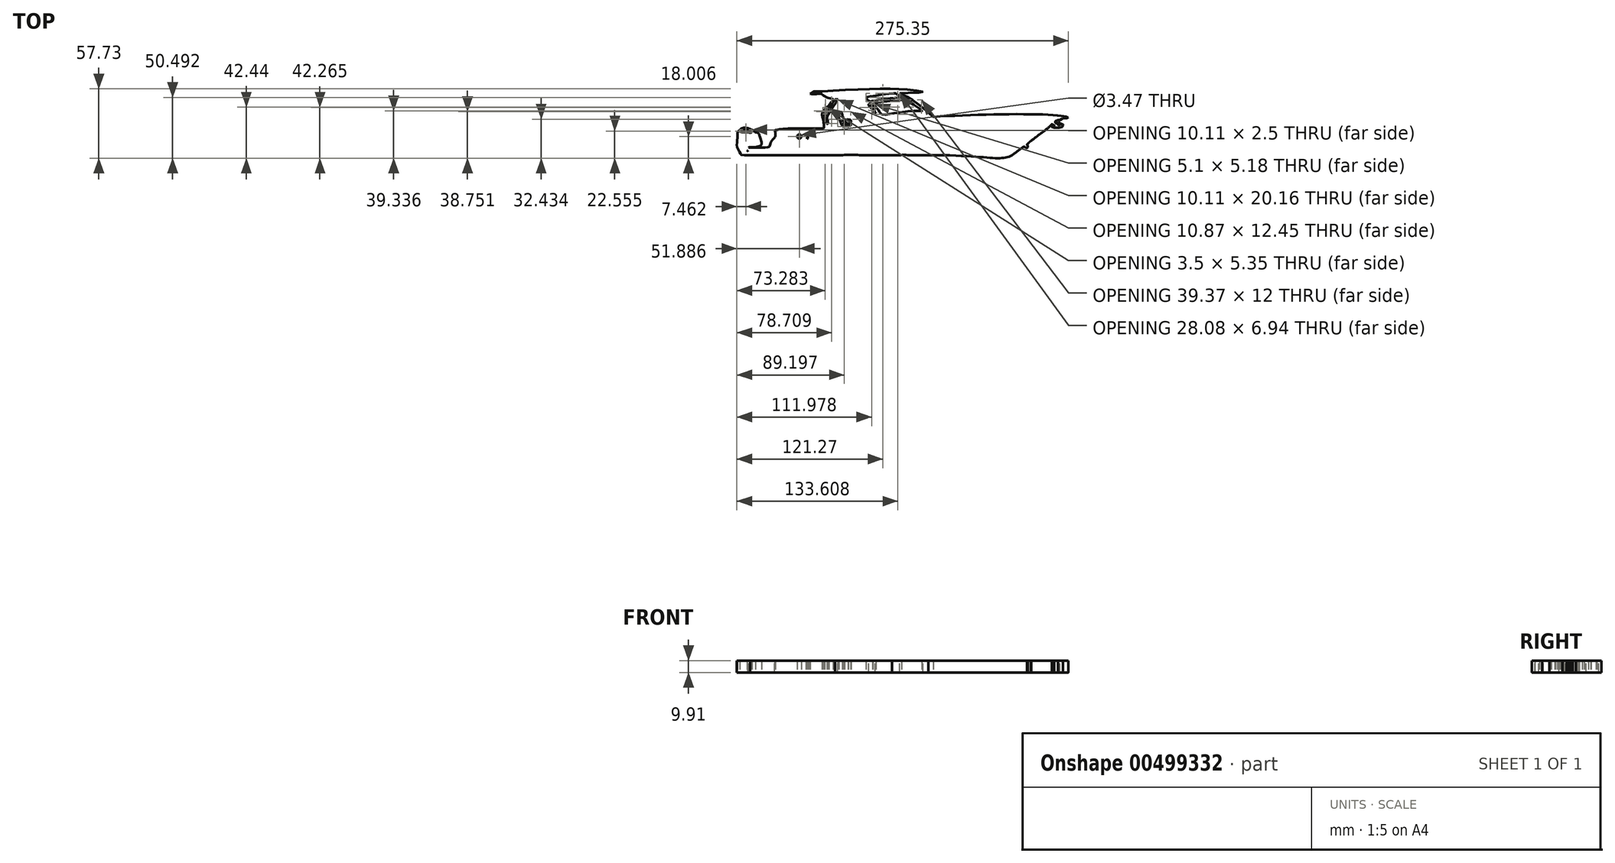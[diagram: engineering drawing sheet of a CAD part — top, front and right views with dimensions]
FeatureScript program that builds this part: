
annotation { "Feature Type Name" : "Feature", "Feature Type Description" : "" }
export const myFeature = defineFeature(function(context is Context, id is Id, definition is map)
    precondition{}
    {
        {
            var Q0;
            Q0=qCreatedBy(makeId("Top.planeOp"),FACE);
            var sketch = newSketch(context, id + "F0", { "sketchPlane" : qUnion([Q0])});
            skFitSpline(sketch, "E0", {"points": [v(181.82, 12.96) * mm, v(177.4, 14.1) * mm, v(69.7, 13.5) * mm, v(25.53, 9.3) * mm, v(19.92, 8.52) * mm], "startDerivative": vector(1.7, -4.6) * mm, "endDerivative": vector(-96.1, -9.77) * mm});
            skFitSpline(sketch, "E1", {"points": [v(19.92, 8.52) * mm, v(11.89, 7.3) * mm, v(0, 4.75) * mm, v(-5.76, 3.64) * mm, v(-21.62, 3.73) * mm, v(-57.86, 3.13) * mm, v(-62.13, 1.85) * mm, v(-60.42, 1.34) * mm, v(-58.8, 1) * mm, v(-52.92, 0.83) * mm, v(-44.65, 0.83) * mm, v(-38.6, 0.91) * mm, v(-28.44, 1) * mm, v(-16.08, 0.83) * mm, v(-10.37, 0.91) * mm, v(-5.5, 0.91) * mm, v(-2.78, 1.42) * mm, v(1.49, 2.79) * mm, v(4.56, 3.64) * mm, v(10.7, 4.66) * mm, v(15.39, 5.6) * mm, v(20.67, 6.46) * mm, v(27.84, 7.48) * mm, v(53.16, 10.3) * mm, v(65.53, 10.8) * mm, v(70.56, 11.23) * mm, v(181.82, 12.96) * mm], "startDerivative": vector(-204.32, -26.46) * mm, "endDerivative": vector(1116.59, 11.05) * mm});
            skFitSpline(sketch, "E2", {"points": [v(150.8, -6.4) * mm, v(136.83, -7.24) * mm, v(77, -11.4) * mm, v(39.07, -13.62) * mm, v(-5.53, -13.97) * mm, v(-32.22, -13.7) * mm, v(-56.7, -13.54) * mm, v(-83.8, -13.7) * mm, v(-84.92, -14.48) * mm, v(-83.04, -15.59) * mm, v(-76.47, -15.59) * mm, v(-57.71, -15.59) * mm, v(-38.53, -16.01) * mm, v(-32.64, -16.01) * mm, v(-7.32, -16.01) * mm, v(12.55, -15.84) * mm, v(72.24, -13.54) * mm, v(94.33, -11.75) * mm, v(106.35, -10.81) * mm, v(150.8, -6.4) * mm]});
            skFitSpline(sketch, "E3", {"points": [v(-62.13, 1.85) * mm, v(-61.49, 0.78) * mm, v(-61.61, -2.84) * mm, v(-63.48, -5.07) * mm, v(-65.9, -9.53) * mm, v(-67.22, -11.64) * mm, v(-83.62, -12) * mm, v(-83.38, -12.3) * mm, v(-83.8, -13.7) * mm], "startDerivative": vector(9.33, -10.43) * mm, "endDerivative": vector(-10.89, -19.72) * mm});
            skFitSpline(sketch, "E4", {"points": [v(-83.62, -12) * mm, v(-73.48, -10.16) * mm, v(-74.45, -2.78) * mm, v(-77.88, 0.76) * mm], "startDerivative": vector(4.15, 3.72) * mm, "endDerivative": vector(-38.38, 8.76) * mm});
            skFitSpline(sketch, "E5", {"points": [v(-77.88, 0.76) * mm, v(-79.82, 1.87) * mm, v(-83.38, 3.86) * mm, v(-86.1, 4.58) * mm, v(-88.98, 3.98) * mm, v(-91.58, 2.29) * mm, v(-92.7, 0.76) * mm, v(-92.95, -2.8) * mm, v(-93.16, -6.9) * mm, v(-93.43, -10.58) * mm, v(-92.18, -13.75) * mm, v(-90.43, -17.3) * mm, v(-89.7, -18.23) * mm, v(-82.47, -18.23) * mm, v(-82.35, -18.23) * mm], "startDerivative": vector(-35.29, 17.01) * mm, "endDerivative": vector(3.35, -0.6) * mm});
            skFitSpline(sketch, "E6", {"points": [v(-84.92, -14.48) * mm, v(-83.04, -16.64) * mm, v(-82.35, -18.23) * mm], "startDerivative": vector(4.12, -3.97) * mm, "endDerivative": vector(0.95, -4.82) * mm});
            skFitSpline(sketch, "E7", {"points": [v(-80.95, 0.76) * mm, v(-88.13, 0.76) * mm, v(-91.05, 1.27) * mm, v(-89.24, 2.99) * mm, v(-80.95, 0.76) * mm]});
            skFitSpline(sketch, "E8", {"points": [v(149.26, -7.8) * mm, v(147.28, -7.83) * mm, v(113.55, -11.96) * mm, v(83.7, -15.93) * mm, v(65.63, -18.23) * mm, v(43.16, -18.23) * mm, v(35.36, -18.23) * mm, v(37.32, -17.46) * mm, v(40.05, -16.74) * mm, v(43.16, -16.7) * mm, v(43.2, -17.38) * mm], "startDerivative": vector(-28.19, 2) * mm, "endDerivative": vector(-7.93, -28.97) * mm});
            skFitSpline(sketch, "E9", {"points": [v(35.36, -18.23) * mm, v(6.92, -18.23) * mm, v(-5.49, -18.23) * mm, v(-12.01, -18.23) * mm, v(-9.45, -17.33) * mm, v(-8.43, -17.16) * mm, v(-5.53, -17.12) * mm], "startDerivative": vector(-93.99, -0.34) * mm, "endDerivative": vector(31.9, 0.18) * mm});
            skFitSpline(sketch, "E10", {"points": [v(-5.53, -17.12) * mm, v(-5.49, -18.23) * mm], "startDerivative": vector(0.04, -1.11) * mm, "endDerivative": vector(0.04, -1.11) * mm});
            skFitSpline(sketch, "E11", {"points": [v(-12.01, -18.23) * mm, v(-82.35, -18.23) * mm], "startDerivative": vector(-70.34, 0) * mm, "endDerivative": vector(-70.34, 0) * mm});
            skFitSpline(sketch, "E12", {"points": [v(-32.53, 32.61) * mm, v(-29.39, 34.74) * mm, v(-27.97, 34.64) * mm, v(-1.6, 35.86) * mm, v(31.66, 36.87) * mm, v(52.65, 35.66) * mm, v(60.76, 33.83) * mm, v(41.9, 33.02) * mm, v(43.22, 32.3) * mm, v(51.33, 27.95) * mm, v(61.47, 20.65) * mm, v(69.7, 13.5) * mm], "startDerivative": vector(69.06, 54.52) * mm, "endDerivative": vector(89.04, -78.05) * mm});
            skFitSpline(sketch, "E13", {"points": [v(-32.53, 32.61) * mm, v(-26.45, 32.61) * mm, v(-23.5, 32.61) * mm, v(-18.94, 29.77) * mm, v(-13.47, 27.98) * mm, v(-16.91, 22.68) * mm], "startDerivative": vector(30.81, -1.19) * mm, "endDerivative": vector(-8.73, -35.9) * mm});
            skFitSpline(sketch, "E14", {"points": [v(-16.91, 22.68) * mm, v(-19.75, 20.65) * mm, v(-22.6, 15.68) * mm, v(-21.98, 11.93) * mm, v(-21.17, 4.73) * mm, v(-21.62, 3.73) * mm], "startDerivative": vector(-14.92, -8.12) * mm, "endDerivative": vector(-5.25, -6.4) * mm});
            skFitSpline(sketch, "E15", {"points": [v(-18.44, 21.16) * mm, v(-20.8, 18.68) * mm, v(-22.04, 16.19) * mm, v(-21.62, 15.68) * mm, v(-20.23, 17.88) * mm, v(-18.44, 21.16) * mm]});
            skFitSpline(sketch, "E16", {"points": [v(-9.7, 27.98) * mm, v(-11.33, 27.98) * mm, v(-20.28, 13.5) * mm, v(-19.94, 11.75) * mm, v(-18.94, 7.75) * mm, v(-17.85, 7.92) * mm, v(-18.44, 11.84) * mm, v(-18.44, 13.5) * mm, v(-16.91, 16.62) * mm, v(-9.96, 27.1) * mm, v(-9.7, 27.98) * mm]});
            skFitSpline(sketch, "E17", {"points": [v(-9.7, 27.98) * mm, v(-5.44, 32.9) * mm, v(-3.74, 33.33) * mm, v(4.36, 33.24) * mm, v(6.07, 32.14) * mm, v(10.59, 28.8) * mm, v(12.12, 27.98) * mm, v(14.77, 25.31) * mm, v(15.8, 24.3) * mm, v(15.53, 23.18) * mm, v(17.58, 21.05) * mm, v(19.97, 19.09) * mm, v(22.19, 18.51) * mm, v(23.9, 16.79) * mm, v(19.37, 17.55) * mm, v(18.43, 16.79) * mm, v(15.36, 14.06) * mm, v(13.06, 12.52) * mm, v(8.46, 11.5) * mm, v(8.54, 10.05) * mm, v(8.37, 7.4) * mm, v(-4.85, 5.62) * mm, v(-5.61, 5.36) * mm], "startDerivative": vector(75.6, 96.22) * mm, "endDerivative": vector(-15.4, -12.16) * mm});
            skFitSpline(sketch, "E18", {"points": [v(-8.77, 17.8) * mm, v(-9.7, 16.87) * mm, v(-5.61, 5.36) * mm], "startDerivative": vector(-4.93, -2.36) * mm, "endDerivative": vector(8.91, -19.64) * mm});
            skFitSpline(sketch, "E19", {"points": [v(1.49, 2.79) * mm, v(10.57, 2.79) * mm, v(29.44, 2.79) * mm, v(48.6, 3.64) * mm, v(74.48, 3.64) * mm, v(166.01, 5.23) * mm], "startDerivative": vector(71.82, 0.39) * mm, "endDerivative": vector(290.97, 6.55) * mm});
            skFitSpline(sketch, "E20", {"points": [v(26.77, 15.59) * mm, v(34.58, 16.15) * mm, v(41.48, 17.07) * mm, v(55.63, 18.51) * mm, v(60.25, 18.51) * mm, v(48.31, 27.11) * mm, v(46.42, 27.9) * mm, v(19.37, 24.28) * mm, v(19.74, 23.5) * mm, v(22.19, 21.5) * mm, v(24.66, 18.51) * mm, v(26.77, 15.59) * mm]});
            skFitSpline(sketch, "E21", {"points": [v(13.76, 29.24) * mm, v(16.86, 26.33) * mm, v(18.89, 26.53) * mm, v(27.64, 28.2) * mm, v(41.98, 29.67) * mm, v(43.34, 30.05) * mm, v(38.46, 33.01) * mm, v(38.1, 33.25) * mm, v(14.63, 29.92) * mm, v(13.76, 29.24) * mm]});
            skFitSpline(sketch, "E22", {"points": [v(-8.77, 17.8) * mm, v(-7.56, 17.8) * mm, v(-6.18, 17.08) * mm, v(-5.74, 15.7) * mm, v(-5.85, 14.54) * mm, v(-5.43, 13.78) * mm, v(-4.73, 12.96) * mm, v(-4.47, 12.29) * mm, v(-4.18, 10.85) * mm, v(-4.5, 10.05) * mm, v(-5.42, 9.95) * mm, v(-5.63, 10.2) * mm, v(-5.48, 9.7) * mm, v(-4.47, 9.56) * mm, v(-4.33, 9.04) * mm, v(-4.55, 8.18) * mm, v(-4.93, 7.57) * mm, v(-4.44, 7.36) * mm, v(-3.33, 7.46) * mm, v(-2.87, 7.5) * mm, v(-2.04, 7.44) * mm, v(-1.18, 7.36) * mm, v(-1.4, 7.87) * mm, v(-1.56, 8.67) * mm, v(-2.61, 8.38) * mm, v(-3.14, 8.38) * mm, v(-3.5, 8.96) * mm, v(-3.95, 9.81) * mm, v(-3.88, 10.36) * mm, v(-3.47, 10.77) * mm, v(-2.85, 11.05) * mm, v(-2.42, 11.23) * mm, v(-2.3, 11.3) * mm, v(-1.62, 11.36) * mm, v(-0.73, 11.34) * mm, v(0, 11.25) * mm, v(0.28, 11.23) * mm, v(0.86, 10.96) * mm, v(1.2, 10.38) * mm, v(1.3, 9.67) * mm, v(1.05, 8.97) * mm, v(0.64, 8.35) * mm, v(-0.37, 8.13) * mm, v(-0.7, 8.7) * mm, v(-0.38, 7.64) * mm, v(0, 7.49) * mm, v(0.33, 7.58) * mm, v(0.9, 7.25) * mm, v(1.24, 6.7) * mm, v(1.16, 5.96) * mm], "startDerivative": vector(43.94, 4.5) * mm, "endDerivative": vector(-8.27, -37.04) * mm});
            skFitSpline(sketch, "E23", {"points": [v(-8.5, 27.45) * mm, v(-4.26, 32.27) * mm, v(2.23, 32.52) * mm, v(4.94, 32.45) * mm, v(7.6, 30.05) * mm, v(9.97, 28) * mm, v(10.6, 27.5) * mm, v(11.35, 27.71) * mm, v(12.43, 26.32) * mm, v(13.95, 24.87) * mm, v(14.8, 23.32) * mm, v(15.48, 21.77) * mm, v(17.68, 19.4) * mm, v(19.91, 18.22) * mm, v(21.15, 17.96) * mm, v(22.02, 17.02) * mm, v(19.37, 17.55) * mm], "startDerivative": vector(33.9, 59.8) * mm, "endDerivative": vector(-58.09, 18.3) * mm});
            skFitSpline(sketch, "E24", {"points": [v(16.21, 24.28) * mm, v(16.2, 22.81) * mm, v(17.02, 21.99) * mm, v(19.65, 19.25) * mm, v(21.28, 19.16) * mm, v(16.21, 24.28) * mm]});
            skFitSpline(sketch, "E25", {"points": [v(135.07, -18.23) * mm, v(65.63, -18.23) * mm], "startDerivative": vector(-70.36, -0.54) * mm, "endDerivative": vector(-70.36, -0.54) * mm});
            skFitSpline(sketch, "E26", {"points": [v(181.82, 12.96) * mm, v(181.8, 12.56) * mm, v(177.64, 12.46) * mm, v(176.2, 11.71) * mm, v(174.48, 10.62) * mm, v(172.8, 10.68) * mm, v(170.42, 9.1) * mm, v(172.64, 8.01) * mm, v(174.17, 8.9) * mm, v(174.76, 8.64) * mm, v(173.59, 7.73) * mm, v(173.23, 7.42) * mm, v(173.27, 6.7) * mm, v(173.5, 6.44) * mm, v(176.84, 7.94) * mm, v(177.07, 5.59) * mm, v(174.73, 4.6) * mm, v(168.22, 4.86) * mm, v(168.71, 5.13) * mm, v(169.93, 5.44) * mm, v(170.02, 6.69) * mm, v(168.84, 7.1) * mm, v(168.39, 7.48) * mm, v(166.01, 5.23) * mm, v(147.56, -9.34) * mm, v(147.8, -10.15) * mm, v(147.89, -11.95) * mm, v(146.26, -12.14) * mm, v(145.13, -11.3) * mm, v(135.07, -18.23) * mm, v(65.63, -18.23) * mm], "startDerivative": vector(13.7, -37.03) * mm, "endDerivative": vector(-923.69, 0) * mm});
            skLineSegment(sketch, "E27", {"start": v(111.62, -18.42) * mm, "end": v(141.39, -13.6) * mm});
            skLineSegment(sketch, "E28", {"start": v(122, -18.29) * mm, "end": v(141.39, -13.6) * mm});
            skLineSegment(sketch, "E29", {"start": v(-46.8, -1.33) * mm, "end": v(-47.04, -1.92) * mm});
            skFitSpline(sketch, "E30", {"points": [v(-46.8, -1.33) * mm, v(-46.97, -1.26) * mm, v(-47.3, -1.15) * mm, v(-47.4, -1.13) * mm, v(-47.5, -1.11) * mm, v(-47.64, -1.1) * mm, v(-47.75, -1.1) * mm, v(-47.87, -1.09) * mm, v(-47.96, -1.1) * mm, v(-48.07, -1.1) * mm, v(-48.15, -1.12) * mm, v(-48.25, -1.14) * mm, v(-48.38, -1.18) * mm, v(-48.5, -1.24) * mm, v(-48.63, -1.32) * mm, v(-48.74, -1.41) * mm, v(-48.85, -1.56) * mm, v(-48.9, -1.65) * mm, v(-48.94, -1.78) * mm, v(-48.97, -1.94) * mm, v(-48.97, -2.17) * mm, v(-48.92, -2.4) * mm, v(-48.8, -2.63) * mm, v(-48.6, -2.83) * mm, v(-48.04, -3.15) * mm, v(-47.77, -3.28) * mm, v(-47.59, -3.42) * mm, v(-47.52, -3.53) * mm, v(-47.5, -3.63) * mm, v(-47.5, -3.74) * mm, v(-47.57, -3.88) * mm, v(-47.72, -3.97) * mm, v(-47.97, -4) * mm, v(-48.28, -3.98) * mm, v(-48.57, -3.9) * mm, v(-49, -3.73) * mm, v(-49.01, -3.73) * mm, v(-49.02, -3.87) * mm, v(-49.01, -4.27) * mm, v(-49.02, -4.4) * mm, v(-49, -4.4) * mm, v(-48.98, -4.42) * mm, v(-48.88, -4.46) * mm, v(-48.44, -4.58) * mm, v(-48.02, -4.6) * mm, v(-47.63, -4.57) * mm, v(-47.46, -4.52) * mm, v(-47.17, -4.38) * mm, v(-46.92, -4.14) * mm, v(-46.82, -3.89) * mm, v(-46.78, -3.58) * mm, v(-46.84, -3.25) * mm, v(-47.05, -2.94) * mm, v(-47.3, -2.76) * mm, v(-47.64, -2.57) * mm, v(-48.05, -2.36) * mm, v(-48.2, -2.23) * mm, v(-48.25, -2.16) * mm, v(-48.26, -2) * mm, v(-48.2, -1.84) * mm, v(-48.04, -1.72) * mm, v(-47.83, -1.7) * mm, v(-47.62, -1.71) * mm, v(-47.04, -1.92) * mm], "startDerivative": vector(-9.43, 4.04) * mm, "endDerivative": vector(23.9, -8.1) * mm});
            skFitSpline(sketch, "E31", {"points": [v(-43.7, -1.33) * mm, v(-43.94, -1.92) * mm], "startDerivative": vector(-0.25, -0.57) * mm, "endDerivative": vector(-0.25, -0.57) * mm});
            skFitSpline(sketch, "E32", {"points": [v(-43.94, -1.92) * mm, v(-44.25, -1.78) * mm, v(-44.61, -1.7) * mm, v(-44.96, -1.73) * mm, v(-45.23, -1.88) * mm, v(-45.32, -1.98) * mm, v(-45.44, -2.16) * mm, v(-45.53, -2.46) * mm, v(-45.56, -2.67) * mm, v(-45.57, -2.89) * mm, v(-45.56, -3.09) * mm, v(-45.52, -3.3) * mm, v(-45.47, -3.49) * mm, v(-45.33, -3.75) * mm, v(-45.06, -3.94) * mm, v(-44.73, -4) * mm, v(-44.46, -3.98) * mm, v(-43.84, -3.83) * mm], "startDerivative": vector(-4.7, 2.25) * mm, "endDerivative": vector(7.82, 2.16) * mm});
            skLineSegment(sketch, "E33", {"start": v(-43.84, -3.83) * mm, "end": v(-43.84, -4.43) * mm});
            skFitSpline(sketch, "E34", {"points": [v(-43.84, -4.43) * mm, v(-44.06, -4.51) * mm, v(-44.2, -4.55) * mm, v(-44.38, -4.58) * mm, v(-44.65, -4.6) * mm, v(-44.85, -4.6) * mm, v(-44.98, -4.6) * mm, v(-45.18, -4.57) * mm, v(-45.4, -4.5) * mm, v(-45.58, -4.42) * mm, v(-46, -4.07) * mm, v(-46.18, -3.72) * mm, v(-46.29, -3.26) * mm, v(-46.31, -2.92) * mm, v(-46.3, -2.62) * mm, v(-46.22, -2.16) * mm, v(-46.17, -2.03) * mm, v(-46, -1.73) * mm, v(-45.86, -1.54) * mm, v(-45.57, -1.3) * mm, v(-45.36, -1.2) * mm, v(-45.08, -1.12) * mm, v(-44.77, -1.09) * mm, v(-44.55, -1.1) * mm, v(-44.3, -1.13) * mm, v(-43.7, -1.33) * mm], "startDerivative": vector(-6.48, -2.34) * mm, "endDerivative": vector(11.04, -4.1) * mm});
            skCircle(sketch, "E35", {"center": v(-41.58, -2.84) * mm, "radius": 1.74 * mm});
            skFitSpline(sketch, "E36", {"points": [v(-41.58, -1.7) * mm, v(-41.83, -1.71) * mm, v(-42.17, -1.85) * mm, v(-42.38, -2.16) * mm, v(-42.5, -2.73) * mm, v(-42.47, -3.27) * mm, v(-42.24, -3.75) * mm, v(-41.74, -4) * mm, v(-41.23, -3.92) * mm, v(-40.9, -3.58) * mm, v(-40.77, -3.03) * mm, v(-40.81, -2.31) * mm, v(-41.1, -1.84) * mm, v(-41.38, -1.71) * mm, v(-41.58, -1.7) * mm]});
            skLineSegment(sketch, "E37", {"start": v(-39.33, -1.16) * mm, "end": v(-39.33, -3.4) * mm});
            skLineSegment(sketch, "E38", {"start": v(-39.32, -1.16) * mm, "end": v(-38.59, -1.16) * mm});
            skLineSegment(sketch, "E39", {"start": v(-38.59, -1.17) * mm, "end": v(-38.59, -3.4) * mm});
            skLineSegment(sketch, "E40", {"start": v(-37.22, -1.15) * mm, "end": v(-37.22, -3.4) * mm});
            skLineSegment(sketch, "E41", {"start": v(-36.5, -1.18) * mm, "end": v(-36.5, -3.4) * mm});
            skLineSegment(sketch, "E42", {"start": v(-37.22, -1.15) * mm, "end": v(-36.5, -1.12) * mm});
            skFitSpline(sketch, "E43", {"points": [v(-38.59, -3.38) * mm, v(-38.53, -3.58) * mm, v(-38.41, -3.84) * mm, v(-37.95, -4) * mm, v(-37.57, -3.94) * mm, v(-37.3, -3.73) * mm, v(-37.22, -3.4) * mm], "startDerivative": vector(0.44, -1.44) * mm, "endDerivative": vector(0.28, 2.1) * mm});
            skFitSpline(sketch, "E44", {"points": [v(-39.33, -3.4) * mm, v(-39.27, -3.77) * mm, v(-39.06, -4.18) * mm, v(-38.66, -4.47) * mm, v(-37.94, -4.63) * mm, v(-37.3, -4.5) * mm, v(-36.94, -4.32) * mm, v(-36.61, -3.92) * mm, v(-36.52, -3.6) * mm, v(-36.5, -3.4) * mm], "startDerivative": vector(0.26, -3.61) * mm, "endDerivative": vector(0.14, 2.67) * mm});
            skLineSegment(sketch, "E45", {"start": v(-35.98, -1.13) * mm, "end": v(-35.98, -1.73) * mm});
            skLineSegment(sketch, "E46", {"start": v(-35.98, -1.73) * mm, "end": v(-35.08, -1.73) * mm});
            skLineSegment(sketch, "E47", {"start": v(-35.08, -1.73) * mm, "end": v(-35.07, -4.6) * mm});
            skLineSegment(sketch, "E48", {"start": v(-35.07, -4.6) * mm, "end": v(-34.37, -4.58) * mm});
            skLineSegment(sketch, "E49", {"start": v(-34.37, -4.58) * mm, "end": v(-34.34, -1.77) * mm});
            skLineSegment(sketch, "E50", {"start": v(-34.34, -1.77) * mm, "end": v(-33.42, -1.76) * mm});
            skLineSegment(sketch, "E51", {"start": v(-33.42, -1.76) * mm, "end": v(-33.42, -1.14) * mm});
            skLineSegment(sketch, "E52", {"start": v(-33.42, -1.14) * mm, "end": v(-35.98, -1.14) * mm});
            skSolve(sketch);
        }
        {
            var Q0;
            Q0 = qSketchRegion(id + "F0", true);
            var Q1;
            {var subQ5=sQuery(id+"F0.wireOp",EDGE,"1e78bd7b-3a0e-4be7-80bb-0a9c4fdda6ef.sketch_text.stroke-50");var subQ6=sQuery(id+"F0.wireOp",EDGE,"1e78bd7b-3a0e-4be7-80bb-0a9c4fdda6ef.sketch_text.stroke-43");var subQ7=makeQuery(id+"F0.imprint","INTERSECT",VERTEX,{"derivedFrom":[subQ6,subQ5]});Q1=makeQuery(id+"F0.imprint","IMPRINT",FACE,{"disambiguationData":[TD([[makeQuery(id+"F0.imprint","IMPRINT",EDGE,{"disambiguationData":[TD([[subQ7,-1.0]])],"derivedFrom":subQ6}),-1.0]])]});}
            extrude(context, id + "F1", {"entities" : qUnion([Q0, Q1]), "depth" : 9.9 * mm, "offsetDistance" : 25.4 * mm});
        }
    });
